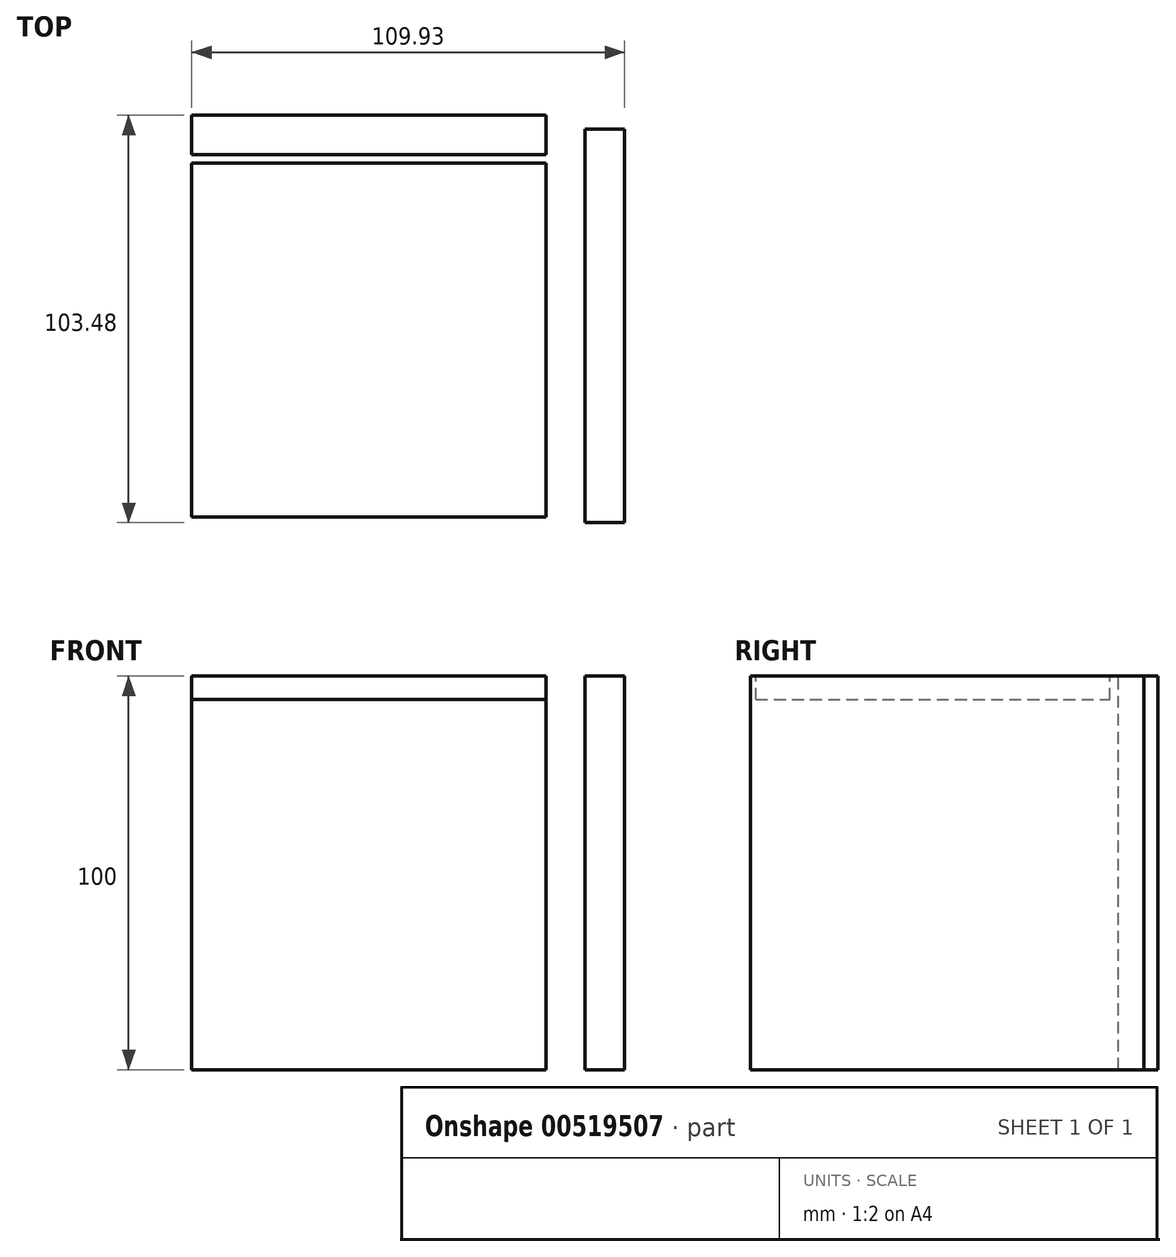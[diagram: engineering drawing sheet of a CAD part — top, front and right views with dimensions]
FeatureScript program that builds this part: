
annotation { "Feature Type Name" : "Feature", "Feature Type Description" : "" }
export const myFeature = defineFeature(function(context is Context, id is Id, definition is map)
    precondition{}
    {
        {
            var Q0;
            Q0=qCreatedBy(makeId("Top.planeOp"),FACE);
            var sketch = newSketch(context, id + "F0", { "sketchPlane" : qUnion([Q0])});
            skLineSegment(sketch, "E0.bottom", {"start": v(-61.71, -64.01) * mm, "end": v(28.29, -64.01) * mm});
            skLineSegment(sketch, "E0.top", {"start": v(-61.71, 25.99) * mm, "end": v(28.29, 25.99) * mm});
            skLineSegment(sketch, "E0.left", {"start": v(-61.71, -64.01) * mm, "end": v(-61.71, 25.99) * mm});
            skLineSegment(sketch, "E0.right", {"start": v(28.29, -64.01) * mm, "end": v(28.29, 25.99) * mm});
            skSolve(sketch);
        }
        {
            var Q0;
            Q0=makeQuery(id+"F0.imprint","IMPRINT",FACE,{"disambiguationData":[TD([[makeQuery(id+"F0.imprint","IMPRINT",EDGE,{"derivedFrom":sQuery(id+"F0.wireOp",EDGE,"E0.bottom")}),1.0]])]});
            extrude(context, id + "F1", {"entities" : qUnion([Q0]), "oppositeDirection" : true, "depth" : 6 * mm, "offsetDistance" : 25 * mm});
        }
        {
            var Q0;
            Q0=qCreatedBy(makeId("Top.planeOp"),FACE);
            var sketch = newSketch(context, id + "F2", { "sketchPlane" : qUnion([Q0])});
            skLineSegment(sketch, "E1.bottom", {"start": v(38.22, -65.4) * mm, "end": v(48.22, -65.4) * mm});
            skLineSegment(sketch, "E1.top", {"start": v(38.22, 34.6) * mm, "end": v(48.22, 34.6) * mm});
            skLineSegment(sketch, "E1.left", {"start": v(38.22, -65.4) * mm, "end": v(38.22, 34.6) * mm});
            skLineSegment(sketch, "E1.right", {"start": v(48.22, -65.4) * mm, "end": v(48.22, 34.6) * mm});
            skSolve(sketch);
        }
        {
            var Q0;
            Q0=makeQuery(id+"F2.imprint","IMPRINT",FACE,{"disambiguationData":[TD([[makeQuery(id+"F2.imprint","IMPRINT",EDGE,{"derivedFrom":sQuery(id+"F2.wireOp",EDGE,"E1.bottom")}),1.0]])]});
            extrude(context, id + "F3", {"entities" : qUnion([Q0]), "oppositeDirection" : true, "depth" : 100 * mm, "offsetDistance" : 25 * mm});
        }
        {
            var Q0;
            Q0=qCreatedBy(makeId("Top.planeOp"),FACE);
            var sketch = newSketch(context, id + "F4", { "sketchPlane" : qUnion([Q0])});
            skLineSegment(sketch, "E2.bottom", {"start": v(-61.71, 28.1) * mm, "end": v(28.29, 28.1) * mm});
            skLineSegment(sketch, "E2.top", {"start": v(-61.71, 38.1) * mm, "end": v(28.29, 38.1) * mm});
            skLineSegment(sketch, "E2.left", {"start": v(-61.71, 28.1) * mm, "end": v(-61.71, 38.1) * mm});
            skLineSegment(sketch, "E2.right", {"start": v(28.29, 28.1) * mm, "end": v(28.29, 38.1) * mm});
            skSolve(sketch);
        }
        {
            var Q0;
            Q0=makeQuery(id+"F4.imprint","IMPRINT",FACE,{"disambiguationData":[TD([[makeQuery(id+"F4.imprint","IMPRINT",EDGE,{"derivedFrom":sQuery(id+"F4.wireOp",EDGE,"E2.bottom")}),1.0]])]});
            extrude(context, id + "F5", {"entities" : qUnion([Q0]), "oppositeDirection" : true, "depth" : 100 * mm, "offsetDistance" : 25 * mm});
        }
    });
